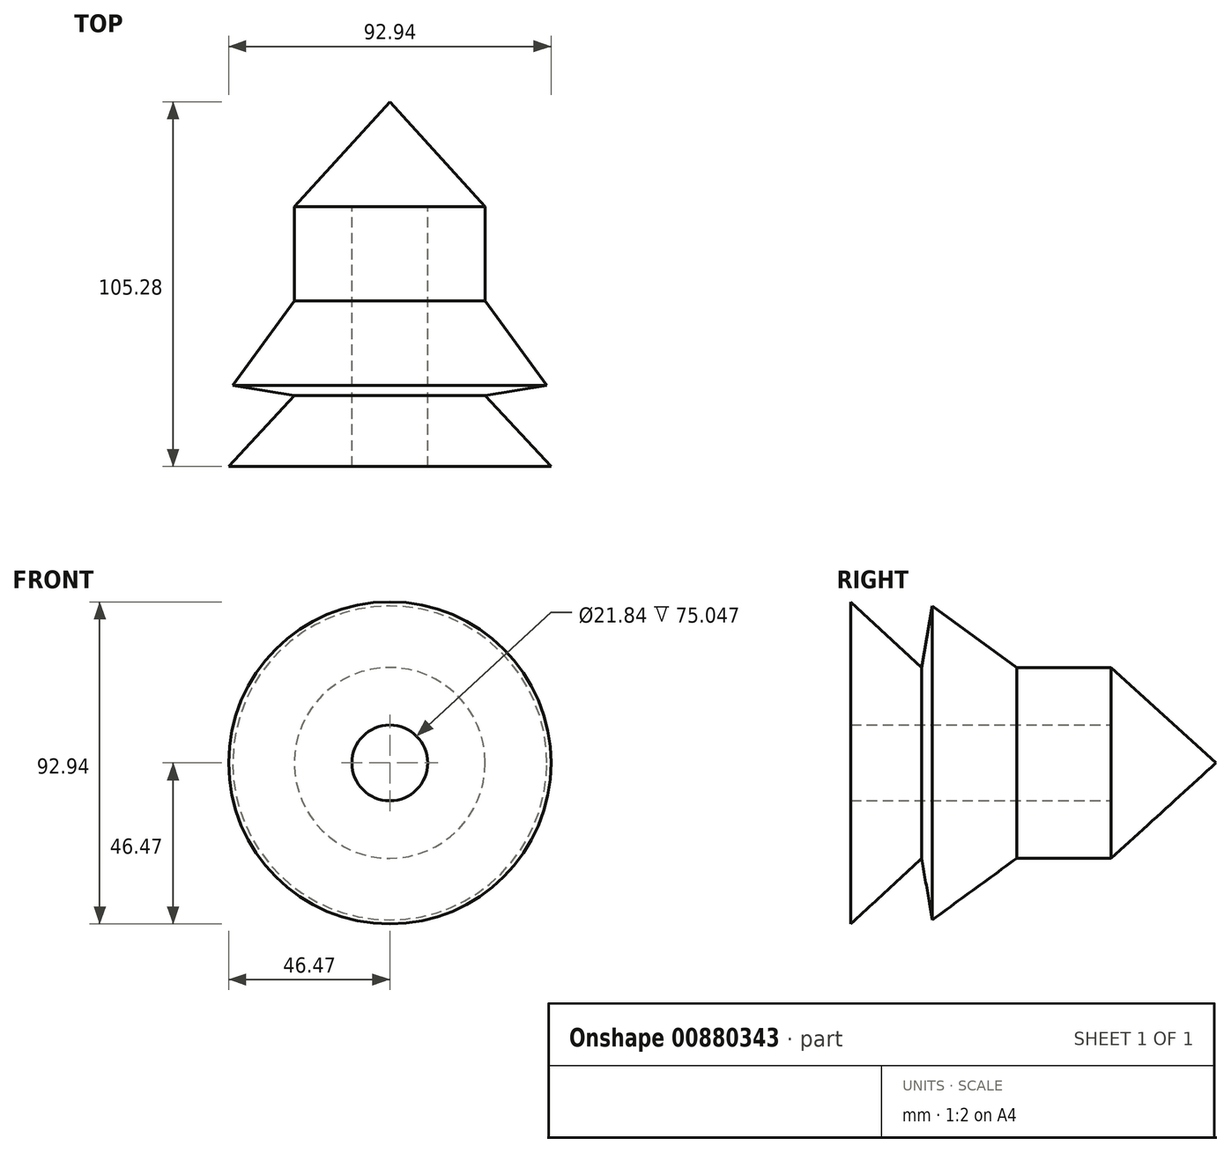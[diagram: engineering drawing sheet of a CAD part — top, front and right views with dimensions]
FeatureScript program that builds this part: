
annotation { "Feature Type Name" : "Feature", "Feature Type Description" : "" }
export const myFeature = defineFeature(function(context is Context, id is Id, definition is map)
    precondition{}
    {
        {
            var Q0;
            Q0=qCreatedBy(makeId("Top.planeOp"),FACE);
            var sketch = newSketch(context, id + "F0", { "sketchPlane" : qUnion([Q0])});
            skLineSegment(sketch, "E0", {"start": v(46.47, -75.05) * mm, "end": v(27.52, -54.6) * mm});
            skLineSegment(sketch, "E1", {"start": v(27.52, 0) * mm, "end": v(0, 30.23) * mm});
            skLineSegment(sketch, "E2", {"start": v(27.52, 0) * mm, "end": v(27.52, -27.22) * mm});
            skLineSegment(sketch, "E3", {"start": v(27.52, -27.22) * mm, "end": v(45.27, -51.59) * mm});
            skLineSegment(sketch, "E4", {"start": v(45.27, -51.59) * mm, "end": v(27.52, -54.6) * mm});
            skLineSegment(sketch, "E5", {"start": v(46.47, -75.05) * mm, "end": v(0, -75.05) * mm});
            skLineSegment(sketch, "E6", {"start": v(0, -75.05) * mm, "end": v(0, 30.23) * mm});
            skSolve(sketch);
        }
        {
            var Q0;
            Q0=makeQuery(id+"F0.imprint","IMPRINT",FACE,{"disambiguationData":[TD([[makeQuery(id+"F0.imprint","IMPRINT",EDGE,{"derivedFrom":sQuery(id+"F0.wireOp",EDGE,"E0")}),1.0]])]});
            var Q1;
            Q1=sQuery(id+"F0.wireOp",EDGE,"E6");
            revolve(context, id + "F1", {"surfaceOperationType" : NewSurfaceOperationType.NEW, "entities" : qUnion([Q0]), "axis" : qUnion([Q1]), "revolveType" : RevolveType.FULL});
        }
        {
            var Q0;
            Q0=qCreatedBy(makeId("Front.planeOp"),FACE);
            var sketch = newSketch(context, id + "F2", { "sketchPlane" : qUnion([Q0])});
            skCircle(sketch, "E7", {"center": v(0, 0) * mm, "radius": 10.92 * mm});
            skSolve(sketch);
        }
        {
            var Q0;
            Q0 = qSketchRegion(id + "F2", true);
            extrude(context, id + "F3", {"entities" : qUnion([Q0]), "operationType" : NewBodyOperationType.REMOVE, "depth" : 429.26 * mm, "offsetDistance" : 25.4 * mm});
        }
    });
